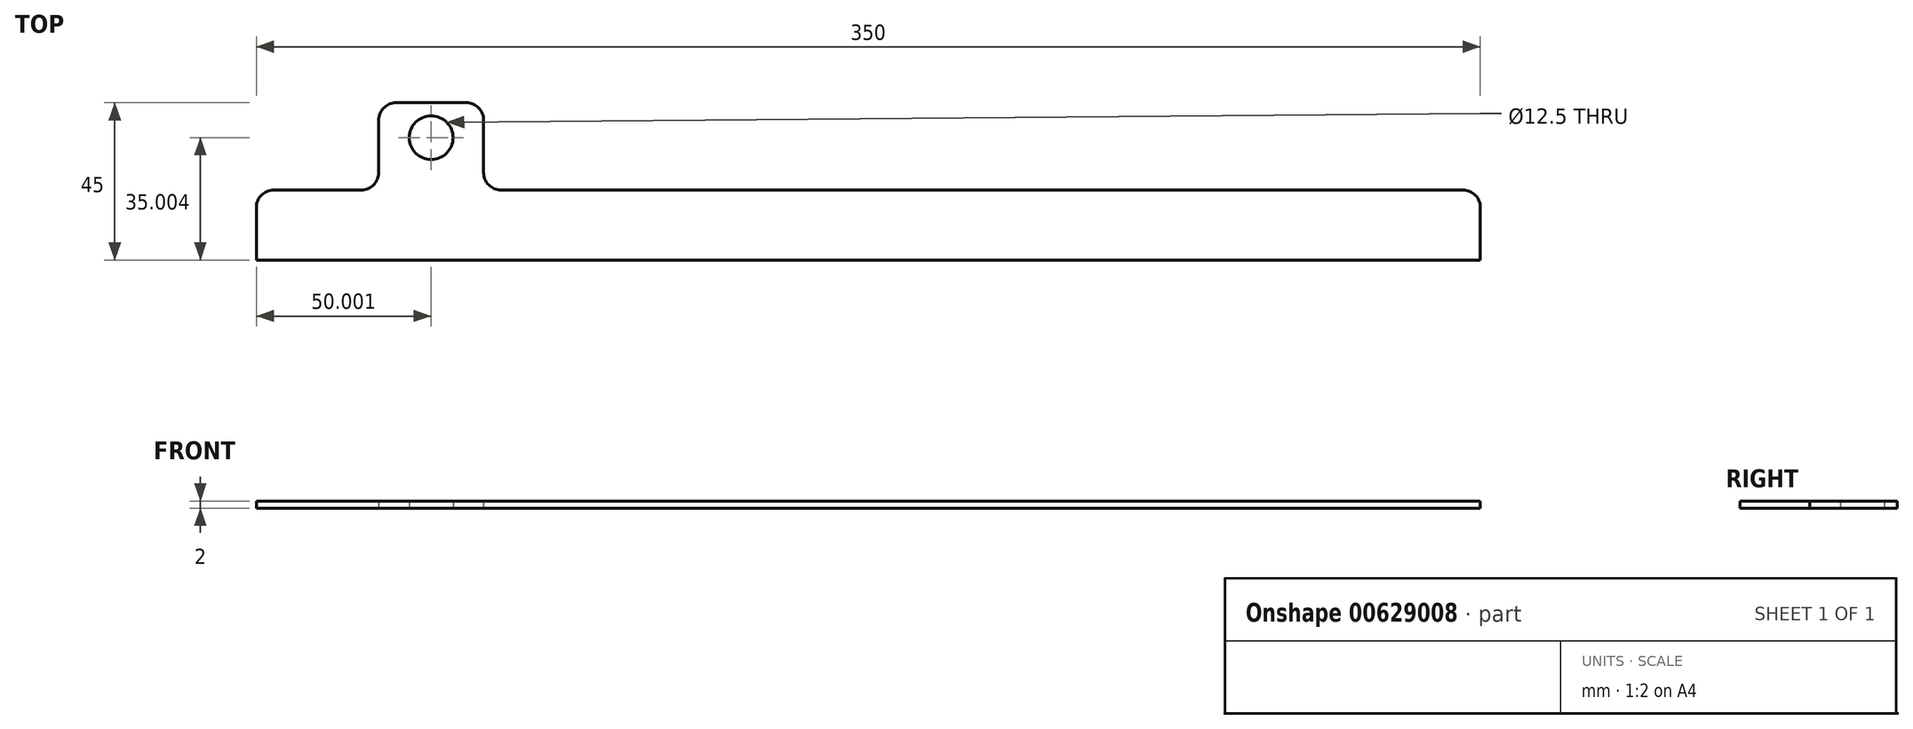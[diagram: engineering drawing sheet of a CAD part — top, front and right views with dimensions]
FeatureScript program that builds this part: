
annotation { "Feature Type Name" : "Feature", "Feature Type Description" : "" }
export const myFeature = defineFeature(function(context is Context, id is Id, definition is map)
    precondition{}
    {
        {
            var Q0;
            Q0=qCreatedBy(makeId("Top.planeOp"),FACE);
            var sketch = newSketch(context, id + "F0", { "sketchPlane" : qUnion([Q0])});
            skLineSegment(sketch, "E0.bottom", {"start": v(-15, 60.67) * mm, "end": v(335, 60.67) * mm});
            skLineSegment(sketch, "E0.top", {"start": v(-15, 40.67) * mm, "end": v(335, 40.67) * mm});
            skLineSegment(sketch, "E0.left", {"start": v(-15, 60.67) * mm, "end": v(-15, 40.67) * mm});
            skLineSegment(sketch, "E0.right", {"start": v(335, 60.67) * mm, "end": v(335, 40.67) * mm});
            skLineSegment(sketch, "E1", {"start": v(-15, 60.67) * mm, "end": v(20, 60.67) * mm});
            skLineSegment(sketch, "E2", {"start": v(20, 60.67) * mm, "end": v(50, 60.67) * mm});
            skLineSegment(sketch, "E3", {"start": v(20, 60.67) * mm, "end": v(20, 85.67) * mm});
            skLineSegment(sketch, "E4", {"start": v(20, 85.67) * mm, "end": v(50, 85.67) * mm});
            skLineSegment(sketch, "E5", {"start": v(50, 60.67) * mm, "end": v(50, 85.67) * mm});
            skLineSegment(sketch, "E6", {"start": v(35, 85.67) * mm, "end": v(35, 75.67) * mm});
            skCircle(sketch, "E7", {"center": v(35, 75.67) * mm, "radius": 6.25 * mm});
            skLineSegment(sketch, "E8", {"start": v(20, 60.67) * mm, "end": v(210, 60.67) * mm});
            skLineSegment(sketch, "E9.bottom", {"start": v(210, 60.67) * mm, "end": v(240, 60.67) * mm});
            skLineSegment(sketch, "E9.top", {"start": v(210, 85.67) * mm, "end": v(240, 85.67) * mm});
            skLineSegment(sketch, "E9.left", {"start": v(210, 60.67) * mm, "end": v(210, 85.67) * mm});
            skLineSegment(sketch, "E9.right", {"start": v(240, 60.67) * mm, "end": v(240, 85.67) * mm});
            skLineSegment(sketch, "E10", {"start": v(225, 85.67) * mm, "end": v(225, 75.67) * mm});
            skCircle(sketch, "E11", {"center": v(225, 75.67) * mm, "radius": 6.25 * mm});
            skSolve(sketch);
        }
        {
            var Q0;
            Q0=makeQuery(id+"F0.imprint","IMPRINT",FACE,{"disambiguationData":[TD([[makeQuery(id+"F0.imprint","IMPRINT",EDGE,{"derivedFrom":sQuery(id+"F0.wireOp",EDGE,"E0.bottom")}),-1.0]])]});
            var Q1;
            {var subQ3=sQuery(id+"F0.wireOp",EDGE,"E3");Q1=makeQuery(id+"F0.imprint","IMPRINT",FACE,{"disambiguationData":[TD([[makeQuery(id+"F0.imprint","IMPRINT",EDGE,{"derivedFrom":subQ3}),-1.0]])]});}
            var Q2;
            Q2=makeQuery(id+"F0.imprint","IMPRINT",FACE,{"disambiguationData":[TD([[makeQuery(id+"F0.imprint","IMPRINT",EDGE,{"derivedFrom":sQuery(id+"F0.wireOp",EDGE,"E9.bottom")}),1.0]])]});
            extrude(context, id + "F1", {"entities" : qUnion([Q0, Q1, Q2]), "depth" : 2 * mm, "offsetDistance" : 25 * mm});
        }
        {
            var Q0;
            Q0=makeQuery(id+"F1.opExtrude","SWEPT_EDGE",EDGE,{"disambiguationData":[OSD([sQuery(id+"F0.wireOp",EDGE,"E1"),sQuery(id+"F0.wireOp",EDGE,"E3"),sQuery(id+"F0.wireOp",EDGE,"E8")])]});
            var Q1;
            Q1=makeQuery(id+"F1.opExtrude","SWEPT_EDGE",EDGE,{"disambiguationData":[OSD([sQuery(id+"F0.wireOp",EDGE,"E5"),sQuery(id+"F0.wireOp",EDGE,"E8")])]});
            var Q2;
            Q2=makeQuery(id+"F1.opExtrude","SWEPT_EDGE",EDGE,{"disambiguationData":[OSD([sQuery(id+"F0.wireOp",EDGE,"E8"),sQuery(id+"F0.wireOp",EDGE,"E9.bottom"),sQuery(id+"F0.wireOp",EDGE,"E9.left")])]});
            var Q3;
            Q3=makeQuery(id+"F1.opExtrude","SWEPT_EDGE",EDGE,{"disambiguationData":[OSD([sQuery(id+"F0.wireOp",EDGE,"E0.bottom"),sQuery(id+"F0.wireOp",EDGE,"E9.bottom"),sQuery(id+"F0.wireOp",EDGE,"E9.right")])]});
            var Q4;
            Q4=makeQuery(id+"F1.opExtrude","SWEPT_EDGE",EDGE,{"disambiguationData":[OSD([sQuery(id+"F0.wireOp",EDGE,"E9.top"),sQuery(id+"F0.wireOp",EDGE,"E9.right")])]});
            var Q5;
            Q5=makeQuery(id+"F1.opExtrude","SWEPT_EDGE",EDGE,{"disambiguationData":[OSD([sQuery(id+"F0.wireOp",EDGE,"E9.top"),sQuery(id+"F0.wireOp",EDGE,"E9.left")])]});
            var Q6;
            Q6=makeQuery(id+"F1.opExtrude","SWEPT_EDGE",EDGE,{"disambiguationData":[OSD([sQuery(id+"F0.wireOp",EDGE,"E3"),sQuery(id+"F0.wireOp",EDGE,"E4")])]});
            var Q7;
            Q7=makeQuery(id+"F1.opExtrude","SWEPT_EDGE",EDGE,{"disambiguationData":[OSD([sQuery(id+"F0.wireOp",EDGE,"E4"),sQuery(id+"F0.wireOp",EDGE,"E5")])]});
            fillet(context, id + "F2", {"entities" : qUnion([Q0, Q1, Q2, Q3, Q4, Q5, Q6, Q7]), "radius" : 5 * mm, "tangentPropagation" : true, "allowEdgeOverflow" : false});
        }
    });
